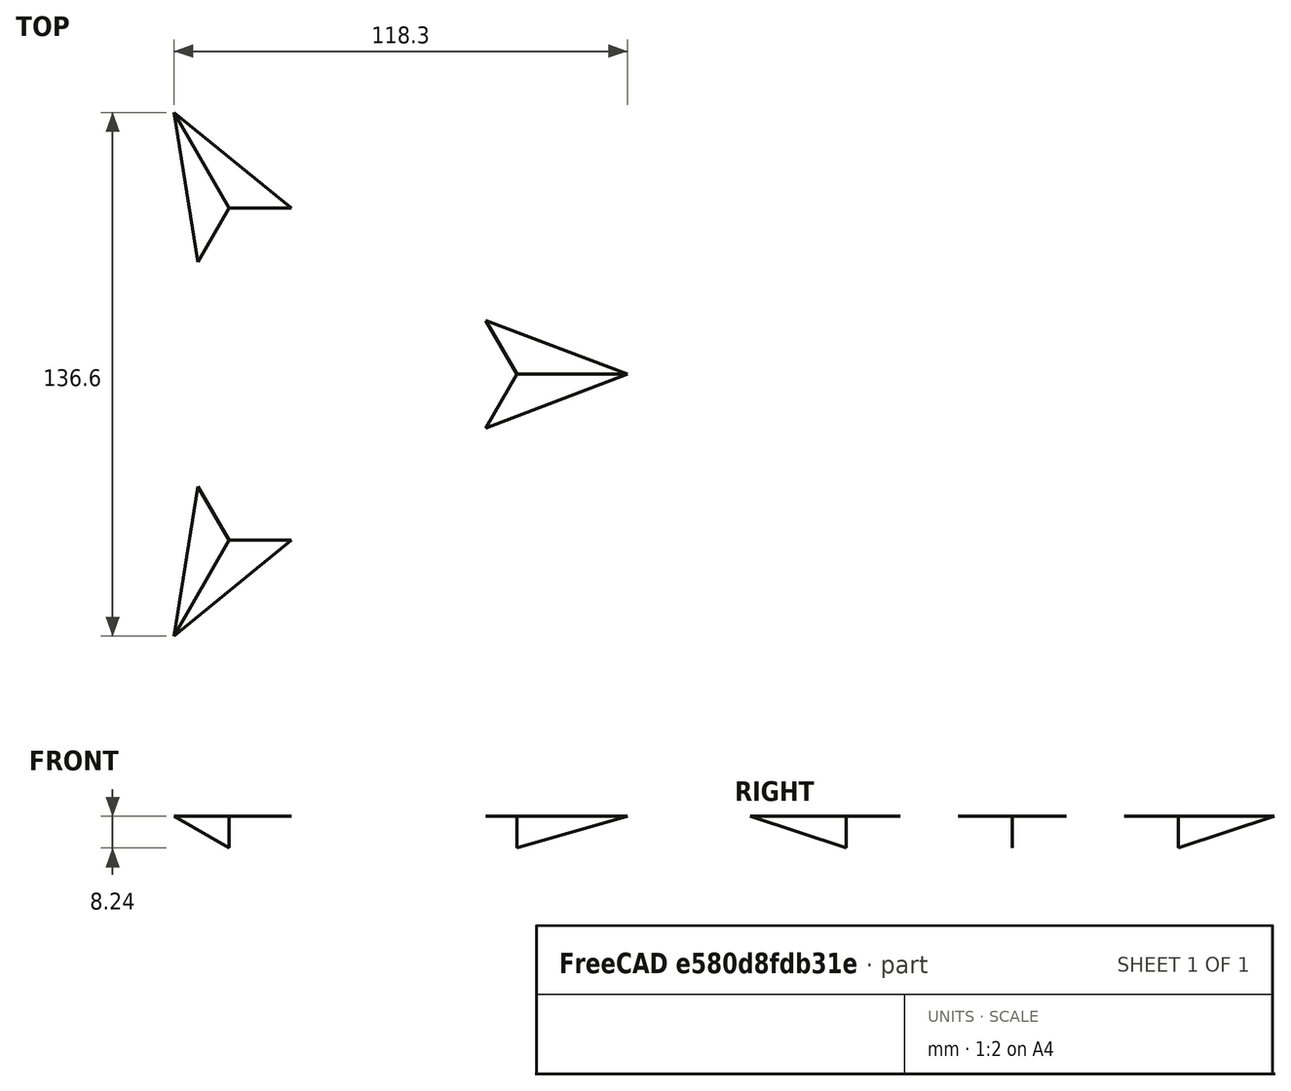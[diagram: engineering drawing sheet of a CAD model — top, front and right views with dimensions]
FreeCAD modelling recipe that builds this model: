
FCSTD DOCUMENT  (FreeCAD 1.1R38827 (Git))
Label: composit_stand3_hat_top_main
License: All rights reserved
LicenseURL: http://en.wikipedia.org/wiki/All_rights_reserved
objects: Part::FeaturePython×3, PartDesign::SubShapeBinder×1, Sketcher::SketchObject×1, Part::Mirroring×1, Part::Compound×1
note: 8 computed .brp shape members not serialized (recipe doc carries the construction recipe); baked Part::Feature solids carry a one-line shape summary decoded from their .brp
EXTERNAL_REF file=composit_stand3_hat_bottom_main.FCStd obj=Sketch
EXTERNAL_REF file=composit_stand3_bar_main.FCStd obj=Sketch
EXTERNAL_REF file=composit_stand3_basement_bottom_main.FCStd obj=Placment

FEATURE [PartDesign::SubShapeBinder] Binder
  BindCopyOnChange = 0
  BindMode = 0
  ClaimChildren = false
  Fuse = false
  MakeFace = true
  OffsetFill = false
  OffsetIntersection = false
  OffsetJoinType = 0
  OffsetOpenResult = false
  PartialLoad = false
  Relative = true
  Support = -> [<external composit_stand3_hat_bottom_main.FCStd>#Sketch]
  _Version = 2
FEATURE [Sketcher::SketchObject] Sketch
  ArcFitTolerance = 0
  FullyConstrained = true
  MakeInternals = false
  expr: Constraints[19] = <<composit_stand3_bar_main>>#<<base_Sketch>>.Constraints.length
  expr: Constraints[6] = <<composit_stand3_basement_bottom_main>>#<<bar_placement>>.Placement.Base.x - 3 mm
  expr: Constraints[7] = <<composit_stand3_bar_main>>#<<base_Sketch>>.Constraints.width / 2 - (2 mm + 1.5 mm)
  sketch-geometry (7):
    g0: LineSegment StartX=379 StartY=0 StartZ=0 EndX=379 EndY=12.8 EndZ=0
    g1: ArcOfCircle CenterX=377 CenterY=12.8 CenterZ=0 NormalX=0 NormalY=0 NormalZ=1 AngleXU=0 Radius=2 StartAngle=3e-16 EndAngle=1.5708
    g2: LineSegment [constr] StartX=0 StartY=0 StartZ=0 EndX=55.8318 EndY=96.7035 EndZ=0
    g3: ArcOfCircle CenterX=361.5 CenterY=626.136 CenterZ=0 NormalX=0 NormalY=0 NormalZ=1 AngleXU=0 Radius=611.336 StartAngle=4.18879 EndAngle=4.71239
    g4: LineSegment [constr] StartX=0 StartY=14.8 StartZ=0 EndX=361.5 EndY=14.8 EndZ=0
    g5: LineSegment StartX=361.5 StartY=14.8 StartZ=0 EndX=377 EndY=14.8 EndZ=0
    g6: LineSegment [constr] StartX=377 StartY=14.8 StartZ=0 EndX=380.5 EndY=14.8 EndZ=0
  constraints (20):
    c: PointOnObject(g4,g-2)
    c: PointOnObject(g0,g-1)
    c: Vertical(g0)
    c: Tangent(g1,g0) = -1.5708
    c: Coincident(g2,g-1)
    c: Angle(g2) = 1.0472
    c: DistanceX(g6) = 380.5
    c: DistanceY(g6) = 14.8
    c: Coincident(g3,g2)
    c: Radius(g1) = 2
    c: Perpendicular(g3,g2)
    c: Coincident(g4,g5)
    c: Horizontal(g4)
    c: Coincident(g5,g6)
    c: Tangent(g5,g1) = 1.5708
    c: DistanceX(g0,g6) = 1.5
    c: Tangent(g3,g4) = -1.5708
    c: Horizontal(g5)
    c: Horizontal(g6)
    c: DistanceX(g3,g6) = 19
FEATURE [Part::Mirroring] Part__Mirroring  label="Sketch (Mirror #1)"
  Base = (0,0,0)
  Normal = (0,1,0)
  Source = -> Sketch
FEATURE [Part::Compound] Compound
  Links = -> [Sketch,Part__Mirroring]
FEATURE [Part::FeaturePython] PolarArray  # WARN: FeaturePython — macro-defined, semantics opaque (R4)
  Alignment = 0
  AttacherType = Attacher::AttachEngine3D
  CellStart = A1
  Count = 3
  DistributionLaw = 0
  EndInclusive = false
  ExposePlacement = false
  FlipX = false
  FlipZ = false
  GeneratorMode = 0
  MarkerShape = 1
  MarkerSize = 0
  NumElements = 3
  OrientMode = 2
  Radius = 50
  Reverse = false
  SpanEnd = 360
  SpanStart = 0
  Step = 120
  Type = lattice2PolarArray2.PolarArray
  UseArcRadius = false
  UseArcRange = 0
  VSGVersion = 1
  Values = 0.0 | 120.0 | 240.0
  ValuesSource = 2
  isLattice = 1
FEATURE [Part::FeaturePython] Populate  label="Populate PolarArray with Compound"  # WARN: FeaturePython — macro-defined, semantics opaque (R4)
  Copying = 0
  ExposePlacement = false
  MarkerShape = 1
  MarkerSize = 0
  NumElements = 0
  Object = -> Compound
  OutputCompounding = 1
  PlacementsTo = -> PolarArray
  Referencing = 1
  Type = lattice2PopulateCopies.LatticePopulateCopies
  isLattice = 0
FEATURE [Part::FeaturePython] Connect  # WARN: FeaturePython — macro-defined, semantics opaque (R4)
  Objects = -> [Populate]
  Tolerance = 0
